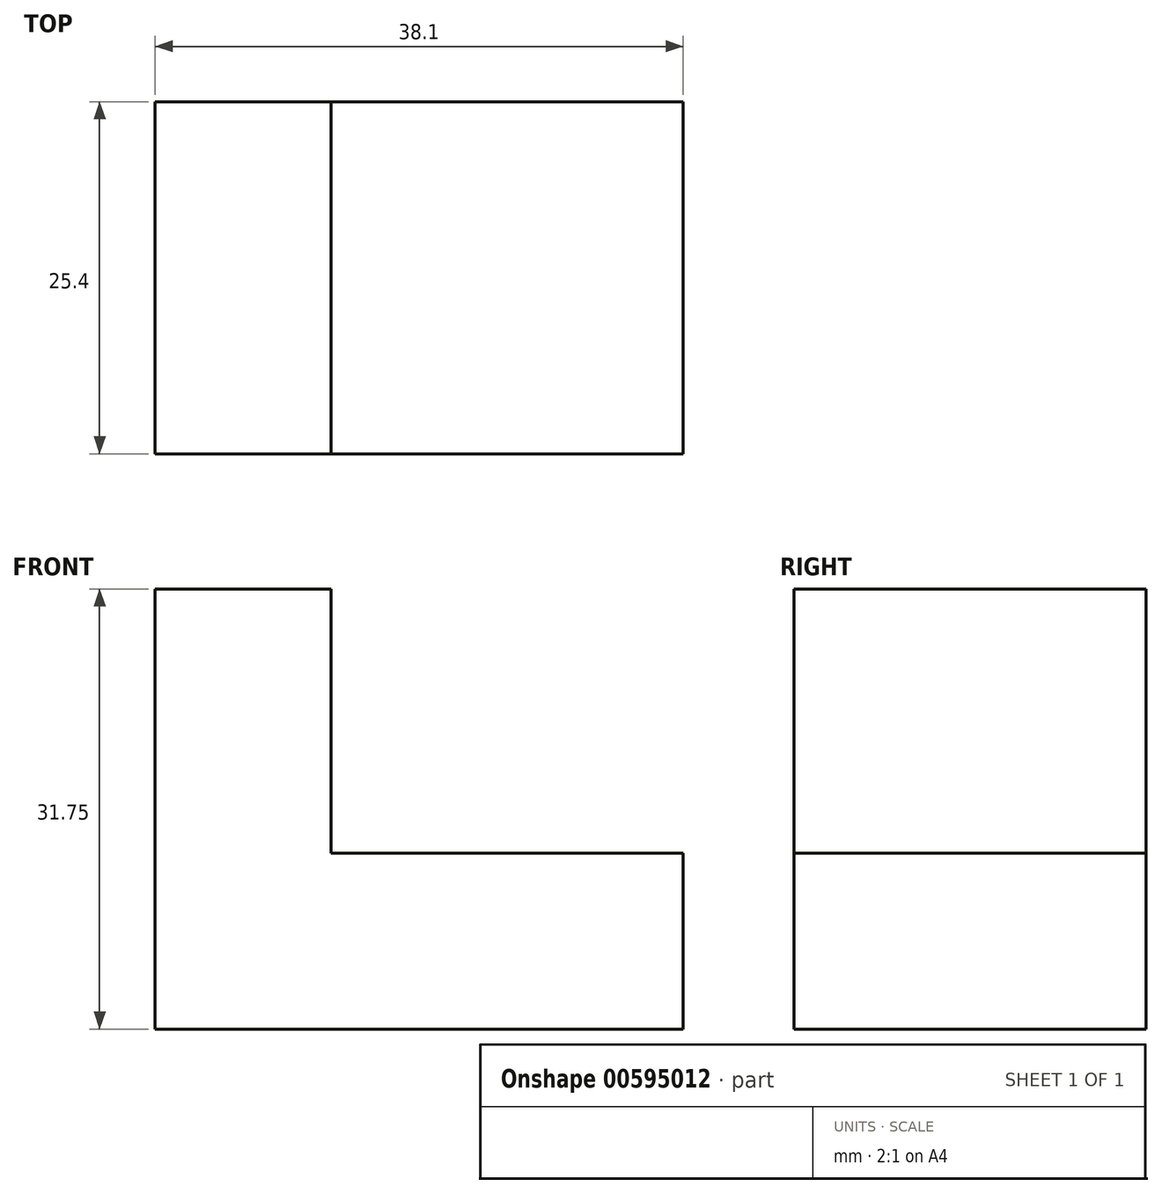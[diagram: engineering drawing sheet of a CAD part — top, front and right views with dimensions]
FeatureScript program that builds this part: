
annotation { "Feature Type Name" : "Feature", "Feature Type Description" : "" }
export const myFeature = defineFeature(function(context is Context, id is Id, definition is map)
    precondition{}
    {
        {
            var Q0;
            Q0=qCreatedBy(makeId("Front.planeOp"),FACE);
            var sketch = newSketch(context, id + "F0", { "sketchPlane" : qUnion([Q0])});
            skLineSegment(sketch, "E0", {"start": v(0, 0) * mm, "end": v(0, 31.75) * mm});
            skLineSegment(sketch, "E1", {"start": v(0, 31.75) * mm, "end": v(12.7, 31.75) * mm});
            skLineSegment(sketch, "E2", {"start": v(12.7, 31.75) * mm, "end": v(12.7, 12.7) * mm});
            skLineSegment(sketch, "E3", {"start": v(12.7, 12.7) * mm, "end": v(38.1, 12.7) * mm});
            skLineSegment(sketch, "E4", {"start": v(38.1, 12.7) * mm, "end": v(38.1, 0) * mm});
            skLineSegment(sketch, "E5", {"start": v(38.1, 0) * mm, "end": v(0, 0) * mm});
            skSolve(sketch);
        }
        {
            var Q0;
            Q0=qCreatedBy(makeId("Front.planeOp"),FACE);
            var sketch = newSketch(context, id + "F1", { "sketchPlane" : qUnion([Q0])});
            skSolve(sketch);
        }
        {
            var Q0;
            Q0 = qSketchRegion(id + "F1", true);
            var Q1;
            Q1=makeQuery(id+"F0.imprint","IMPRINT",FACE,{"disambiguationData":[TD([[makeQuery(id+"F0.imprint","IMPRINT",EDGE,{"derivedFrom":sQuery(id+"F0.wireOp",EDGE,"E0")}),-1.0]])]});
            extrude(context, id + "F2", {"entities" : qUnion([Q0, Q1]), "depth" : 25.4 * mm, "offsetDistance" : 25.4 * mm});
        }
    });
